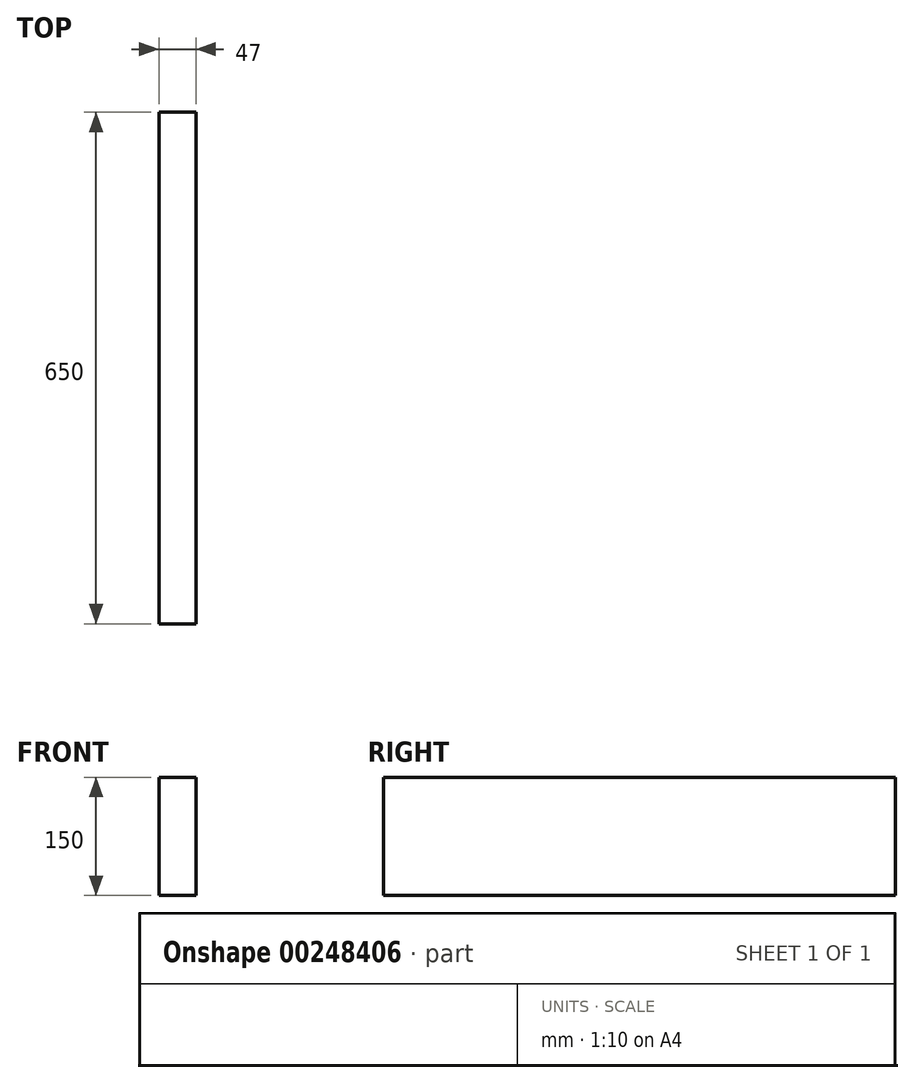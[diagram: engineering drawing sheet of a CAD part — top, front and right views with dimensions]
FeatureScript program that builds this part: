
annotation { "Feature Type Name" : "Feature", "Feature Type Description" : "" }
export const myFeature = defineFeature(function(context is Context, id is Id, definition is map)
    precondition{}
    {
        {
            var Q0;
            Q0=qCreatedBy(makeId("Front.planeOp"),FACE);
            var sketch = newSketch(context, id + "F0", { "sketchPlane" : qUnion([Q0])});
            skLineSegment(sketch, "E0.bottom", {"start": v(0, 0) * mm, "end": v(47, 0) * mm});
            skLineSegment(sketch, "E0.top", {"start": v(0, 150) * mm, "end": v(47, 150) * mm});
            skLineSegment(sketch, "E0.left", {"start": v(0, 0) * mm, "end": v(0, 150) * mm});
            skLineSegment(sketch, "E0.right", {"start": v(47, 0) * mm, "end": v(47, 150) * mm});
            skSolve(sketch);
        }
        {
            var Q0;
            Q0=makeQuery(id+"F0.imprint","IMPRINT",FACE,{"disambiguationData":[TD([[makeQuery(id+"F0.imprint","IMPRINT",EDGE,{"derivedFrom":sQuery(id+"F0.wireOp",EDGE,"E0.bottom")}),1.0]])]});
            extrude(context, id + "F1", {"entities" : qUnion([Q0]), "oppositeDirection" : true, "depth" : 650 * mm});
        }
    });
